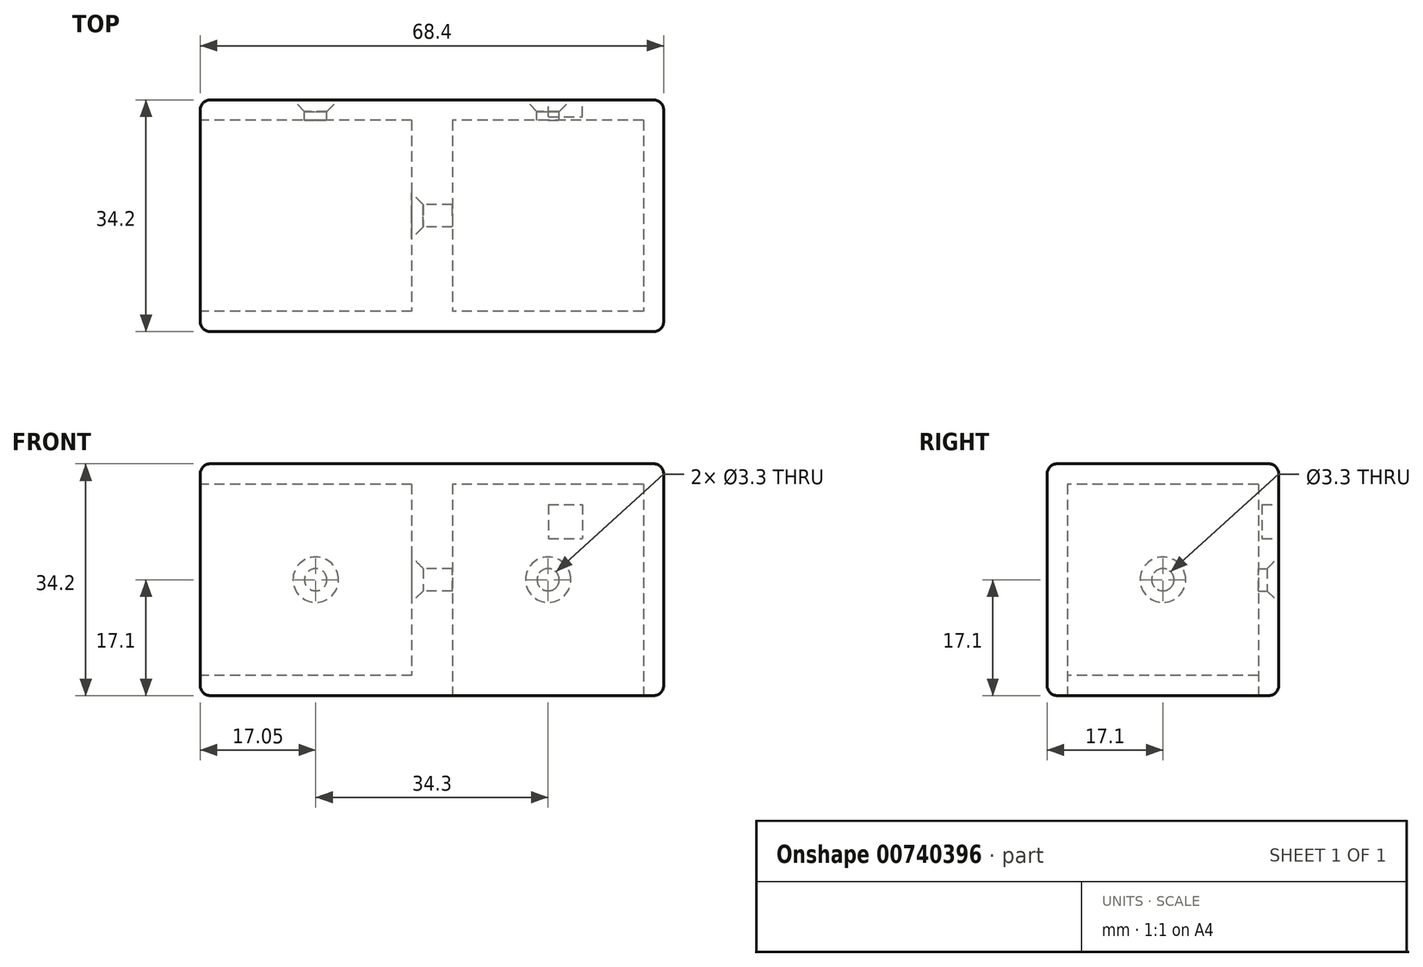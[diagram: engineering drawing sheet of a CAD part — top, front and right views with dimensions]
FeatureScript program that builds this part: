
annotation { "Feature Type Name" : "Feature", "Feature Type Description" : "" }
export const myFeature = defineFeature(function(context is Context, id is Id, definition is map)
    precondition{}
    {
        {
            var Q0;
            Q0=qCreatedBy(makeId("Top.planeOp"),FACE);
            var sketch = newSketch(context, id + "F0", { "sketchPlane" : qUnion([Q0])});
            skLineSegment(sketch, "E0.bottom", {"start": v(-8, 0) * mm, "end": v(-34.2, 0) * mm});
            skLineSegment(sketch, "E0.top", {"start": v(0, 34.2) * mm, "end": v(-34.2, 34.2) * mm});
            skLineSegment(sketch, "E0.left", {"start": v(0, 0) * mm, "end": v(0, 34.2) * mm});
            skLineSegment(sketch, "E0.right", {"start": v(-34.2, 0) * mm, "end": v(-34.2, 34.2) * mm});
            skLineSegment(sketch, "E1", {"start": v(0, 0) * mm, "end": v(-8, 0) * mm});
            skSolve(sketch);
        }
        {
            var Q0;
            Q0=makeQuery(id+"F0.imprint","IMPRINT",FACE,{"disambiguationData":[TD([[makeQuery(id+"F0.imprint","IMPRINT",EDGE,{"derivedFrom":sQuery(id+"F0.wireOp",EDGE,"QRwr5Akg-HTZL-sOMh-trkn-U98YefTGLHnr")}),1.0]])]});
            var Q1;
            Q1=makeQuery(id+"F0.imprint","IMPRINT",FACE,{"disambiguationData":[TD([[makeQuery(id+"F0.imprint","IMPRINT",EDGE,{"derivedFrom":sQuery(id+"F0.wireOp",EDGE,"E0.bottom")}),-1.0]])]});
            extrude(context, id + "F1", {"entities" : qUnion([Q0, Q1]), "depth" : 34.2 * mm, "offsetDistance" : 25 * mm});
        }
        {
            var Q0;
            Q0=makeQuery(id+"F1.opExtrude","SWEPT_FACE",FACE,{"disambiguationData":[OSD([sQuery(id+"F0.wireOp",EDGE,"E0.right")])]});
            var sketch = newSketch(context, id + "F2", { "sketchPlane" : qUnion([Q0])});
            skLineSegment(sketch, "E2.bottom", {"start": v(-34.2, 0) * mm, "end": v(0, 0) * mm});
            skLineSegment(sketch, "E2.top", {"start": v(-34.2, 34.2) * mm, "end": v(0, 34.2) * mm});
            skLineSegment(sketch, "E2.left", {"start": v(-34.2, 0) * mm, "end": v(-34.2, 34.2) * mm});
            skLineSegment(sketch, "E2.right", {"start": v(0, 0) * mm, "end": v(0, 34.2) * mm});
            skSolve(sketch);
        }
        {
            var Q0;
            Q0=qSketchRegion(id+"F2",true);
            extrude(context, id + "F3", {"entities" : qUnion([Q0]), "operationType" : NewBodyOperationType.ADD, "depth" : 34.2 * mm, "offsetDistance" : 25 * mm});
        }
        {
            var Q0;
            Q0=makeQuery(id+"F3.opExtrude","CAP_FACE",FACE,{"disambiguationData":[OSD([sQuery(id+"F2.wireOp",EDGE,"E2.bottom"),sQuery(id+"F2.wireOp",EDGE,"E2.top"),sQuery(id+"F2.wireOp",EDGE,"E2.left"),sQuery(id+"F2.wireOp",EDGE,"E2.right")])],"isStart":false});
            var sketch = newSketch(context, id + "F4", { "sketchPlane" : qUnion([Q0])});
            skLineSegment(sketch, "E3.bottom", {"start": v(-34.2, 34.2) * mm, "end": v(0, 34.2) * mm});
            skLineSegment(sketch, "E3.top", {"start": v(-34.2, 0) * mm, "end": v(0, 0) * mm});
            skLineSegment(sketch, "E3.left", {"start": v(-34.2, 34.2) * mm, "end": v(-34.2, 0) * mm});
            skLineSegment(sketch, "E3.right", {"start": v(0, 34.2) * mm, "end": v(0, 0) * mm});
            skLineSegment(sketch, "E4.0", {"start": v(-31.2, 31.2) * mm, "end": v(-3, 31.2) * mm});
            skLineSegment(sketch, "E4.1", {"start": v(-31.2, 31.2) * mm, "end": v(-31.2, 3) * mm});
            skLineSegment(sketch, "E4.2", {"start": v(-31.2, 3) * mm, "end": v(-3, 3) * mm});
            skLineSegment(sketch, "E4.3", {"start": v(-3, 31.2) * mm, "end": v(-3, 3) * mm});
            skSolve(sketch);
        }
        {
            var Q0;
            Q0=makeQuery(id+"F4.imprint","IMPRINT",FACE,{"disambiguationData":[TD([[makeQuery(id+"F4.imprint","IMPRINT",EDGE,{"derivedFrom":sQuery(id+"F4.wireOp",EDGE,"E4.0")}),-1.0]])]});
            extrude(context, id + "F5", {"entities" : qUnion([Q0]), "operationType" : NewBodyOperationType.REMOVE, "oppositeDirection" : true, "depth" : 31.2 * mm, "offsetDistance" : 25 * mm});
        }
        {
            var Q0;
            Q0=makeQuery(id+"F3.boolean.opBoolean","MERGE",FACE,{"derivedFrom":[makeQuery(id+"F1.opExtrude","SWEPT_FACE",FACE,{"disambiguationData":[OSD([sQuery(id+"F0.wireOp",EDGE,"E0.top")])]}),makeQuery(id+"F3.opExtrude","SWEPT_FACE",FACE,{"disambiguationData":[OSD([sQuery(id+"F2.wireOp",EDGE,"E2.left")])]})]});
            var sketch = newSketch(context, id + "F6", { "sketchPlane" : qUnion([Q0])});
            skPoint(sketch, "E5", {"position": v(17.05, 17.1) * mm});
            skPoint(sketch, "E6", {"position": v(51.35, 17.1) * mm});
            skSolve(sketch);
        }
        {
            var Q0;
            Q0=makeQuery(id+"F5.boolean.opBoolean","COPY",FACE,{"derivedFrom":makeQuery(id+"F5.opExtrude","CAP_FACE",FACE,{"disambiguationData":[OSD([sQuery(id+"F4.wireOp",EDGE,"E4.0"),sQuery(id+"F4.wireOp",EDGE,"E4.1"),sQuery(id+"F4.wireOp",EDGE,"E4.2"),sQuery(id+"F4.wireOp",EDGE,"E4.3")])],"isStart":false})});
            var sketch = newSketch(context, id + "F7", { "sketchPlane" : qUnion([Q0])});
            skPoint(sketch, "E7", {"position": v(-17.1, 17.1) * mm});
            skSolve(sketch);
        }
        {
            var Q0;
            Q0=sQuery(id+"F6.wireOp",VERTEX,"E5");
            var Q1;
            Q1=sQuery(id+"F6.wireOp",VERTEX,"E6");
            var Q2;
            Q2=sQuery(id+"F7.wireOp",VERTEX,"E7");
            var Q3;
            Q3=makeQuery(id+"F1.opExtrude","SWEPT_BODY",BODY,{"disambiguationData":[OSD([sQuery(id+"F0.wireOp",EDGE,"E0.bottom"),sQuery(id+"F0.wireOp",EDGE,"E0.top"),sQuery(id+"F0.wireOp",EDGE,"E0.left"),sQuery(id+"F0.wireOp",EDGE,"E0.right"),sQuery(id+"F0.wireOp",EDGE,"QRwr5Akg-HTZL-sOMh-trkn-U98YefTGLHnr"),sQuery(id+"F0.wireOp",EDGE,"6FfksXsB-Y7vq-xAn0-bQFg-GBrETYwM94Cl"),sQuery(id+"F0.wireOp",EDGE,"N7Ms4oqh-Htai-qQox-I7Rp-QqMJWiCJs41g"),sQuery(id+"F0.wireOp",EDGE,"P6Kv1fKs-vESP-vTW7-nFhL-l93CeoGK7j3d")])]});
            hole(context, id + "F8", {"style" : HoleStyle.C_SINK, "endStyle" : HoleEndStyle.BLIND, "standardTappedOrClearance" : lookupTablePath({ "standard" : "ISO", "fit" : "Normal", "size" : "M3", "type" : "Clearance" }), "standardBlindInLast" : lookupTablePath({ "fit" : "Standard", "standard" : "ISO", "size" : "M3", "type" : "Clearance" }), "holeDiameter" : 3.3 * mm, "cSinkDiameter" : 6.72 * mm, "cSinkAngle" : 90 * degree, "majorDiameter" : 5 * mm, "holeDepth" : 25 * mm, "isTappedThrough" : true, "tappedDepth" : 12 * mm, "tapClearance" : 3, "startFromSketch" : true, "locations" : qUnion([Q0, Q1, Q2]), "scope" : qUnion([Q3])});
        }
        {
            var Q0;
            Q0=makeQuery(id+"F3.boolean.opBoolean","MERGE",FACE,{"derivedFrom":[makeQuery(id+"F1.opExtrude","CAP_FACE",FACE,{"disambiguationData":[OSD([sQuery(id+"F0.wireOp",EDGE,"E0.bottom"),sQuery(id+"F0.wireOp",EDGE,"E0.top"),sQuery(id+"F0.wireOp",EDGE,"E0.left"),sQuery(id+"F0.wireOp",EDGE,"E0.right"),sQuery(id+"F0.wireOp",EDGE,"QRwr5Akg-HTZL-sOMh-trkn-U98YefTGLHnr"),sQuery(id+"F0.wireOp",EDGE,"N7Ms4oqh-Htai-qQox-I7Rp-QqMJWiCJs41g"),sQuery(id+"F0.wireOp",EDGE,"P6Kv1fKs-vESP-vTW7-nFhL-l93CeoGK7j3d")])],"isStart":true}),makeQuery(id+"F3.opExtrude","SWEPT_FACE",FACE,{"disambiguationData":[OSD([sQuery(id+"F2.wireOp",EDGE,"E2.bottom")])]})]});
            var sketch = newSketch(context, id + "F9", { "sketchPlane" : qUnion([Q0])});
            skLineSegment(sketch, "E8.bottom", {"start": v(0, -34.2) * mm, "end": v(-34.2, -34.2) * mm});
            skLineSegment(sketch, "E8.top", {"start": v(0, 0) * mm, "end": v(-34.2, 0) * mm});
            skLineSegment(sketch, "E8.left", {"start": v(0, -34.2) * mm, "end": v(0, 0) * mm});
            skLineSegment(sketch, "E8.right", {"start": v(-34.2, -34.2) * mm, "end": v(-34.2, 0) * mm});
            skLineSegment(sketch, "E9.0", {"start": v(-31.2, -31.2) * mm, "end": v(-31.2, -3) * mm});
            skLineSegment(sketch, "E9.1", {"start": v(-3, -31.2) * mm, "end": v(-31.2, -31.2) * mm});
            skLineSegment(sketch, "E9.2", {"start": v(-3, -31.2) * mm, "end": v(-3, -3) * mm});
            skLineSegment(sketch, "E9.3", {"start": v(-3, -3) * mm, "end": v(-31.2, -3) * mm});
            skSolve(sketch);
        }
        {
            var Q0;
            Q0=makeQuery(id+"F9.imprint","IMPRINT",FACE,{"disambiguationData":[TD([[makeQuery(id+"F9.imprint","IMPRINT",EDGE,{"derivedFrom":sQuery(id+"F9.wireOp",EDGE,"E9.0")}),-1.0]])]});
            extrude(context, id + "F10", {"entities" : qUnion([Q0]), "operationType" : NewBodyOperationType.REMOVE, "oppositeDirection" : true, "depth" : 31.2 * mm, "offsetDistance" : 25 * mm});
        }
        {
            var Q0;
            Q0=makeQuery(id+"F10.boolean.opBoolean","COPY",EDGE,{"derivedFrom":makeQuery(id+"F10.opExtrude","CAP_EDGE",EDGE,{"disambiguationData":[OSD([sQuery(id+"F9.wireOp",EDGE,"E9.0")])],"isStart":true})});
            var Q1;
            Q1=makeQuery(id+"F10.boolean.opBoolean","COPY",EDGE,{"derivedFrom":makeQuery(id+"F10.opExtrude","CAP_EDGE",EDGE,{"disambiguationData":[OSD([sQuery(id+"F9.wireOp",EDGE,"E9.3")])],"isStart":true})});
            var Q2;
            Q2=makeQuery(id+"F10.boolean.opBoolean","COPY",EDGE,{"derivedFrom":makeQuery(id+"F10.opExtrude","CAP_EDGE",EDGE,{"disambiguationData":[OSD([sQuery(id+"F9.wireOp",EDGE,"E9.2")])],"isStart":true})});
            var Q3;
            Q3=makeQuery(id+"F10.boolean.opBoolean","COPY",EDGE,{"derivedFrom":makeQuery(id+"F10.opExtrude","CAP_EDGE",EDGE,{"disambiguationData":[OSD([sQuery(id+"F9.wireOp",EDGE,"E9.1")])],"isStart":true})});
            var Q4;
            Q4=makeQuery(id+"F3.boolean.opBoolean","MERGE",EDGE,{"derivedFrom":[makeQuery(id+"F1.opExtrude","CAP_EDGE",EDGE,{"disambiguationData":[OSD([sQuery(id+"F0.wireOp",EDGE,"E0.top")])],"isStart":true}),makeQuery(id+"F3.opExtrude","SWEPT_EDGE",EDGE,{"disambiguationData":[OSD([sQuery(id+"F2.wireOp",EDGE,"E2.bottom"),sQuery(id+"F2.wireOp",EDGE,"E2.left")])]})]});
            var Q5;
            Q5=makeQuery(id+"F3.boolean.opBoolean","MERGE",EDGE,{"derivedFrom":[makeQuery(id+"F1.opExtrude","CAP_EDGE",EDGE,{"disambiguationData":[OSD([sQuery(id+"F0.wireOp",EDGE,"E0.bottom")])],"isStart":true}),makeQuery(id+"F3.opExtrude","SWEPT_EDGE",EDGE,{"disambiguationData":[OSD([sQuery(id+"F2.wireOp",EDGE,"E2.bottom"),sQuery(id+"F2.wireOp",EDGE,"E2.right")])]})]});
            var Q6;
            Q6=makeQuery(id+"F1.opExtrude","CAP_EDGE",EDGE,{"disambiguationData":[OSD([sQuery(id+"F0.wireOp",EDGE,"E0.left"),sQuery(id+"F0.wireOp",EDGE,"N7Ms4oqh-Htai-qQox-I7Rp-QqMJWiCJs41g")])],"isStart":true});
            var Q7;
            Q7=makeQuery(id+"F3.opExtrude","CAP_EDGE",EDGE,{"disambiguationData":[OSD([sQuery(id+"F2.wireOp",EDGE,"E2.bottom")])],"isStart":false});
            var Q8;
            Q8=makeQuery(id+"F3.opExtrude","CAP_EDGE",EDGE,{"disambiguationData":[OSD([sQuery(id+"F2.wireOp",EDGE,"E2.right")])],"isStart":false});
            var Q9;
            Q9=makeQuery(id+"F3.opExtrude","CAP_EDGE",EDGE,{"disambiguationData":[OSD([sQuery(id+"F2.wireOp",EDGE,"E2.top")])],"isStart":false});
            var Q10;
            Q10=makeQuery(id+"F3.opExtrude","CAP_EDGE",EDGE,{"disambiguationData":[OSD([sQuery(id+"F2.wireOp",EDGE,"E2.left")])],"isStart":false});
            var Q11;
            Q11=makeQuery(id+"F5.boolean.opBoolean","COPY",EDGE,{"derivedFrom":makeQuery(id+"F5.opExtrude","CAP_EDGE",EDGE,{"disambiguationData":[OSD([sQuery(id+"F4.wireOp",EDGE,"E4.0")])],"isStart":true})});
            var Q12;
            Q12=makeQuery(id+"F5.boolean.opBoolean","COPY",EDGE,{"derivedFrom":makeQuery(id+"F5.opExtrude","CAP_EDGE",EDGE,{"disambiguationData":[OSD([sQuery(id+"F4.wireOp",EDGE,"E4.3")])],"isStart":true})});
            var Q13;
            Q13=makeQuery(id+"F5.boolean.opBoolean","COPY",EDGE,{"derivedFrom":makeQuery(id+"F5.opExtrude","CAP_EDGE",EDGE,{"disambiguationData":[OSD([sQuery(id+"F4.wireOp",EDGE,"E4.2")])],"isStart":true})});
            var Q14;
            Q14=makeQuery(id+"F5.boolean.opBoolean","COPY",EDGE,{"derivedFrom":makeQuery(id+"F5.opExtrude","CAP_EDGE",EDGE,{"disambiguationData":[OSD([sQuery(id+"F4.wireOp",EDGE,"E4.1")])],"isStart":true})});
            var Q15;
            Q15=makeQuery(id+"F3.boolean.opBoolean","MERGE",EDGE,{"derivedFrom":[makeQuery(id+"F1.opExtrude","CAP_EDGE",EDGE,{"disambiguationData":[OSD([sQuery(id+"F0.wireOp",EDGE,"E0.bottom")])],"isStart":false}),makeQuery(id+"F3.opExtrude","SWEPT_EDGE",EDGE,{"disambiguationData":[OSD([sQuery(id+"F2.wireOp",EDGE,"E2.top"),sQuery(id+"F2.wireOp",EDGE,"E2.right")])]})]});
            var Q16;
            Q16=makeQuery(id+"F3.boolean.opBoolean","MERGE",EDGE,{"derivedFrom":[makeQuery(id+"F1.opExtrude","CAP_EDGE",EDGE,{"disambiguationData":[OSD([sQuery(id+"F0.wireOp",EDGE,"E0.top")])],"isStart":false}),makeQuery(id+"F3.opExtrude","SWEPT_EDGE",EDGE,{"disambiguationData":[OSD([sQuery(id+"F2.wireOp",EDGE,"E2.top"),sQuery(id+"F2.wireOp",EDGE,"E2.left")])]})]});
            var Q17;
            Q17=makeQuery(id+"F1.opExtrude","CAP_EDGE",EDGE,{"disambiguationData":[OSD([sQuery(id+"F0.wireOp",EDGE,"E0.left"),sQuery(id+"F0.wireOp",EDGE,"N7Ms4oqh-Htai-qQox-I7Rp-QqMJWiCJs41g")])],"isStart":false});
            var Q18;
            Q18=makeQuery(id+"F1.opExtrude","SWEPT_EDGE",EDGE,{"disambiguationData":[OSD([sQuery(id+"F0.wireOp",EDGE,"E0.top"),sQuery(id+"F0.wireOp",EDGE,"E0.left")])]});
            var Q19;
            Q19=makeQuery(id+"F1.opExtrude","SWEPT_EDGE",EDGE,{"disambiguationData":[OSD([sQuery(id+"F0.wireOp",EDGE,"E0.left"),sQuery(id+"F0.wireOp",EDGE,"E1")])]});
            fillet(context, id + "F11", {"entities" : qUnion([Q0, Q1, Q2, Q3, Q4, Q5, Q6, Q7, Q8, Q9, Q10, Q11, Q12, Q13, Q14, Q15, Q16, Q17, Q18, Q19]), "radius" : 1.5 * mm, "tangentPropagation" : true, "allowEdgeOverflow" : false});
        }
        {
            var Q0;
            Q0=makeQuery(id+"F3.boolean.opBoolean","MERGE",FACE,{"derivedFrom":[makeQuery(id+"F1.opExtrude","SWEPT_FACE",FACE,{"disambiguationData":[OSD([sQuery(id+"F0.wireOp",EDGE,"E0.top")])]}),makeQuery(id+"F3.opExtrude","SWEPT_FACE",FACE,{"disambiguationData":[OSD([sQuery(id+"F2.wireOp",EDGE,"E2.left")])]})]});
            var sketch = newSketch(context, id + "F12", { "sketchPlane" : qUnion([Q0])});
            skPoint(sketch, "E10", {"position": v(14.5, 25.7) * mm});
            skLineSegment(sketch, "E11.bottom", {"start": v(17, 28.2) * mm, "end": v(12, 28.2) * mm});
            skLineSegment(sketch, "E11.top", {"start": v(17, 23.2) * mm, "end": v(12, 23.2) * mm});
            skLineSegment(sketch, "E11.left", {"start": v(17, 28.2) * mm, "end": v(17, 23.2) * mm});
            skLineSegment(sketch, "E11.right", {"start": v(12, 28.2) * mm, "end": v(12, 23.2) * mm});
            skSolve(sketch);
        }
        {
            var Q0;
            Q0=makeQuery(id+"F12.imprint","IMPRINT",FACE,{"disambiguationData":[TD([[makeQuery(id+"F12.imprint","IMPRINT",EDGE,{"derivedFrom":sQuery(id+"F12.wireOp",EDGE,"E11.bottom")}),1.0]])]});
            extrude(context, id + "F13", {"entities" : qUnion([Q0]), "operationType" : NewBodyOperationType.REMOVE, "oppositeDirection" : true, "depth" : 2.5 * mm, "offsetDistance" : 25 * mm});
        }
    });
